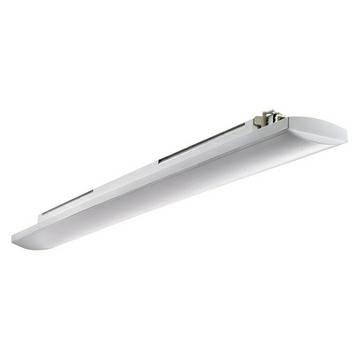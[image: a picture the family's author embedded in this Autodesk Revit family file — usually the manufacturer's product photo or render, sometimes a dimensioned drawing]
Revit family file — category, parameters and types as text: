
# Revit family: Lighting-Industrial-GEWISS-SMART[3]PLUS-WATERTIGHT-LED_OPAL_800mm
name_source: partatom
category: Apparecchi per illuminazione
units: mm (PartAtom-declared; Revit-internal decimal feet)

## family parameters
Condiviso = No
Host = Superficie
Punto di calcolo locali = No
Quota connettore circolare = Usa diametro
Sorgente d'illuminazione = Sì
Taglio con vuoti quando caricato = No
Tipo di parte = Normale

## types (1)
- Lighting-Industrial-GEWISS-SMART[3]PLUS-WATERTIGHT-LED_OPAL_800mm
    Angolo inclinazione = -90.00°
    Application = Indoor
    Carico apparente = 27 VA
    Catalogue = LIGHTING
    Catalogue Range = SMART[3] PLUS
    Colour temperature = 5700 K (CRI > 90)
    Colour temperature: = 5700 K (CRI > 90)
    Commenti sul wattaggio = 27W
    Descrizione = SMART3 PLUS 800 T.W.DALI HE OPAL 9 57
    Efficiency class of integrated LEDs = A ÷ A++
    Electrocod = 2434
    Emetti da lunghezza linea = 700 mm  [stored 2.29659 ft]
    File diagramma fotometrico = GWS3123AP957.IES
    Filtro dei colori = 16777215
    Ganci = GEWISS  - ALLUMINIO
    Glow Wire Test = 850°C
    IDF = ae53e4e2-e5c7-4ff7-9a9e-bbf61f92d9d9
    IDT = 19b5daac-664e-44b9-8ac3-cb33faf625fb
    IP degree = IP66/IP69
    Immagine tipo = GWS3118P.jpg
    Insulation class = II
    Lamp = LED
    Lampada = LED
    Length = 800 mm
    Lumen output (lm) = 2700
    Lunghezza Lampada = 800 mm  [stored 2.62467 ft]
    Modello = GWS3123AP957
    Operating temperature: = -25 +50 °C
    Produttore = GEWISS S.p.A.
    Prospetto di default = 1219 mm
    SEO = Ceiling
    Schermo. = Gewiss - Led Acceso
    Shield type = Opal
    Shock resistance = IK08
    Stampa 1_100 = Sì
    Stampa 1_200 = No
    Struttura = GEWISS - SMART 3 - GRIGIO
    System power = 26 W
    Technical sheet = https://www.gewiss.com
    Type of light source = LED - Not replaceable
    Typology = DALI
    URL = https://www.gewiss.com
    Variazione temperatura colore lampada con luminosità attenuata = <Nessuno>
    Version file RFA = 20.0
    Voltage = 220-240 V
    Warranty = 5 years
    Working temperature = -25 +50 °C

note: [stored X ft] marks values corroborated as IEEE doubles in the binary element streams (Revit-internal decimal feet)
